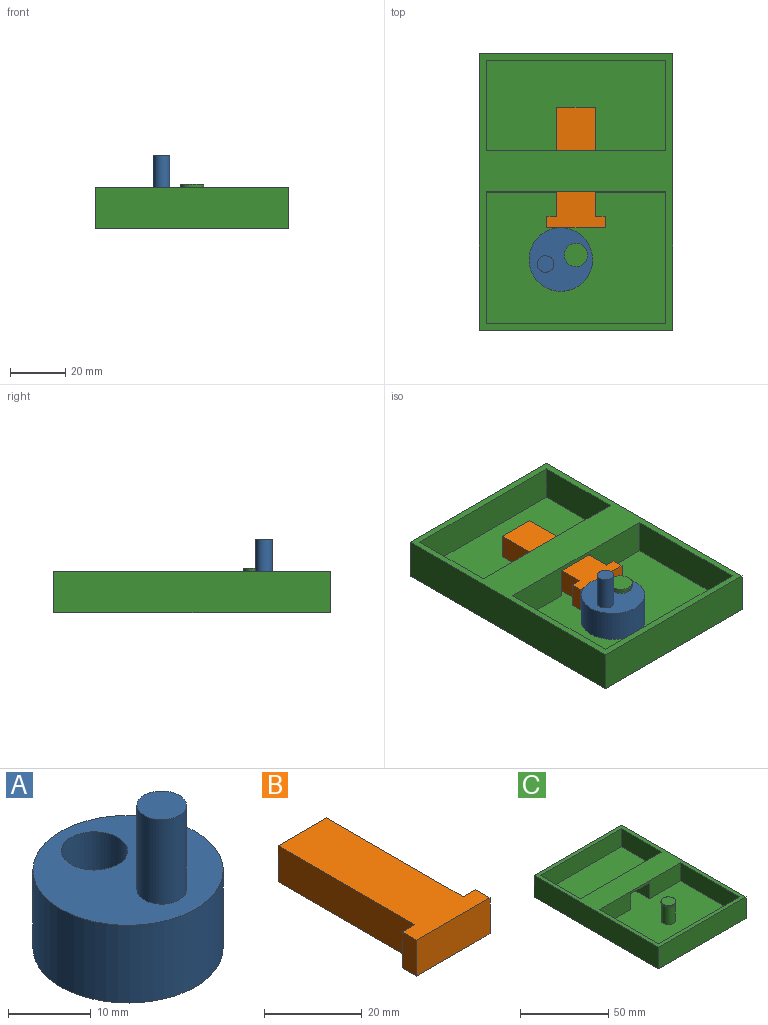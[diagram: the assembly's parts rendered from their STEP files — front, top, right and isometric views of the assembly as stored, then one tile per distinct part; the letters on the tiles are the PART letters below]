
ASSEMBLY  parts=3 mates=3
PART A: 8 faces, bbox 23x23x25 mm
  f0: plane 23x23mm, normal (0,0,1), area 336.9mm2, adj f1,f2,f6
  f1: cylinder r=4mm len=11.5mm, axis (0,0,-1), area 289mm2, adj f0,f3
  f2: cylinder r=11.5mm len=23mm, axis (0,0,-1), area 831mm2, adj f0,f3
  f3: plane 23x23mm, normal (0,0,-1), area 336.9mm2, adj f1,f2,f5
  f4: plane 6x6mm, normal (0,0,-1), area 28.3mm2, adj f5
  f5: cylinder r=3mm len=6mm, axis (0,0,-1), area 18.8mm2, adj f3,f4
  f6: cylinder r=3mm len=12.5mm, axis (0,0,-1), area 235.6mm2, adj f0,f7
  f7: plane 6x6mm, normal (0,0,1), area 28.3mm2, adj f6
PART B: 10 faces, bbox 21.2x43.6x9 mm
  f0: plane 14x9mm, normal (0,1,0), area 126mm2, adj f1,f7,f8,f9
  f1: plane 39.45x9mm, normal (-1,0,0), area 355.1mm2, adj f0,f2,f8,f9
  f2: plane 9x3.6mm, normal (0,1,0), area 32.4mm2, adj f1,f3,f8,f9
  f3: plane 9x4.19mm, normal (-1,0,0), area 37.7mm2, adj f2,f4,f8,f9
  f4: plane 21.2x9mm, normal (0,-1,0), area 190.8mm2, adj f3,f5,f8,f9
  f5: plane 9x4.19mm, normal (1,0,0), area 37.7mm2, adj f4,f6,f8,f9
  f6: plane 9x3.6mm, normal (0,1,0), area 32.4mm2, adj f5,f7,f8,f9
  f7: plane 39.45x9mm, normal (1,0,0), area 355.1mm2, adj f0,f6,f8,f9
  f8: plane 43.64x21.2mm, normal (0,0,1), area 641.1mm2, adj f0,f1,f2,f3,f4,f5,f6,f7
  f9: plane 43.64x21.2mm, normal (0,0,-1), area 641.1mm2, adj f0,f1,f2,f3,f4,f5,f6,f7
PART C: 22 faces, bbox 70x100x16 mm
  f0: plane 47.5x12.5mm, normal (-1,0,0), area 593.8mm2, adj f2,f8,f12,f13
  f1: plane 47.5x12.5mm, normal (1,0,0), area 593.7mm2, adj f2,f8,f12,f13
  f2: plane 100x70mm, normal (0,0,1), area 1800mm2, adj f0,f1,f3,f4,f5,f6,f8,f9
  f3: plane 70x15mm, normal (0,-1,0), area 1050mm2, adj f2,f4,f6,f7
  f4: plane 100x15mm, normal (1,0,0), area 1500mm2, adj f2,f3,f5,f7
  f5: plane 70x15mm, normal (0,1,0), area 1050mm2, adj f2,f4,f6,f7
  f6: plane 100x15mm, normal (-1,0,0), area 1500mm2, adj f2,f3,f5,f7
  f7: plane 100x70mm, normal (0,0,-1), area 7000mm2, adj f3,f4,f5,f6
  f8: plane 65x12.5mm, normal (0,1,0), area 812.5mm2, adj f0,f1,f2,f12
  f9: plane 32.5x12.5mm, normal (-1,0,0), area 406.2mm2, adj f2,f10,f12,f15
  f10: plane 65x12.5mm, normal (0,-1,0), area 812.5mm2, adj f2,f9,f11,f12
  f11: plane 32.5x12.5mm, normal (1,0,0), area 406.2mm2, adj f2,f10,f12,f15
  f12: plane 95x65mm, normal (0,0,1), area 5376mm2, adj f0,f1,f8,f9,f10,f11,f13,f14
  f13: plane 65x12.5mm, normal (0,-1,0), area 647.5mm2, adj f0,f1,f2,f12,f14,f16,f21
  f14: plane 15x11mm, normal (1,0,0), area 165mm2, adj f12,f13,f15,f21
  f15: plane 65x12.5mm, normal (0,1,0), area 647.5mm2, adj f2,f9,f11,f12,f14,f16,f21
  f16: plane 15x11mm, normal (-1,0,0), area 165mm2, adj f12,f13,f15,f21
  f17: cylinder r=3.95mm len=12.5mm, axis (0,0,-1), area 310.2mm2, adj f12,f20
  f18: cylinder r=4.25mm len=8.5mm, axis (0,0,-1), area 26.7mm2, adj f19,f20
  f19: plane 8.5x8.5mm, normal (0,0,1), area 56.7mm2, adj f18
  f20: plane 8.5x8.5mm, normal (0,0,-1), area 7.7mm2, adj f17,f18
  f21: plane 15x15mm, normal (0,0,-1), area 225mm2, adj f13,f14,f15,f16
PLACE A rot(axis=(0,0,-1),73.4deg) t=(21.86,-16.28,-1)mm
PLACE B t=(0,-0.93,0.75)mm
PLACE C at identity fixed
MATE slider B.f0 <-> C.f10  axis (0,1,0) through (0,30.68,8.75)mm
MATE planar C.f12 <-> A.f3  axis (0,0,1) through (0,-0.84,2.5)mm
MATE cylindrical C.f17 <-> A.f1  axis (0,0,-1) through (0,-22.82,2.5)mm
